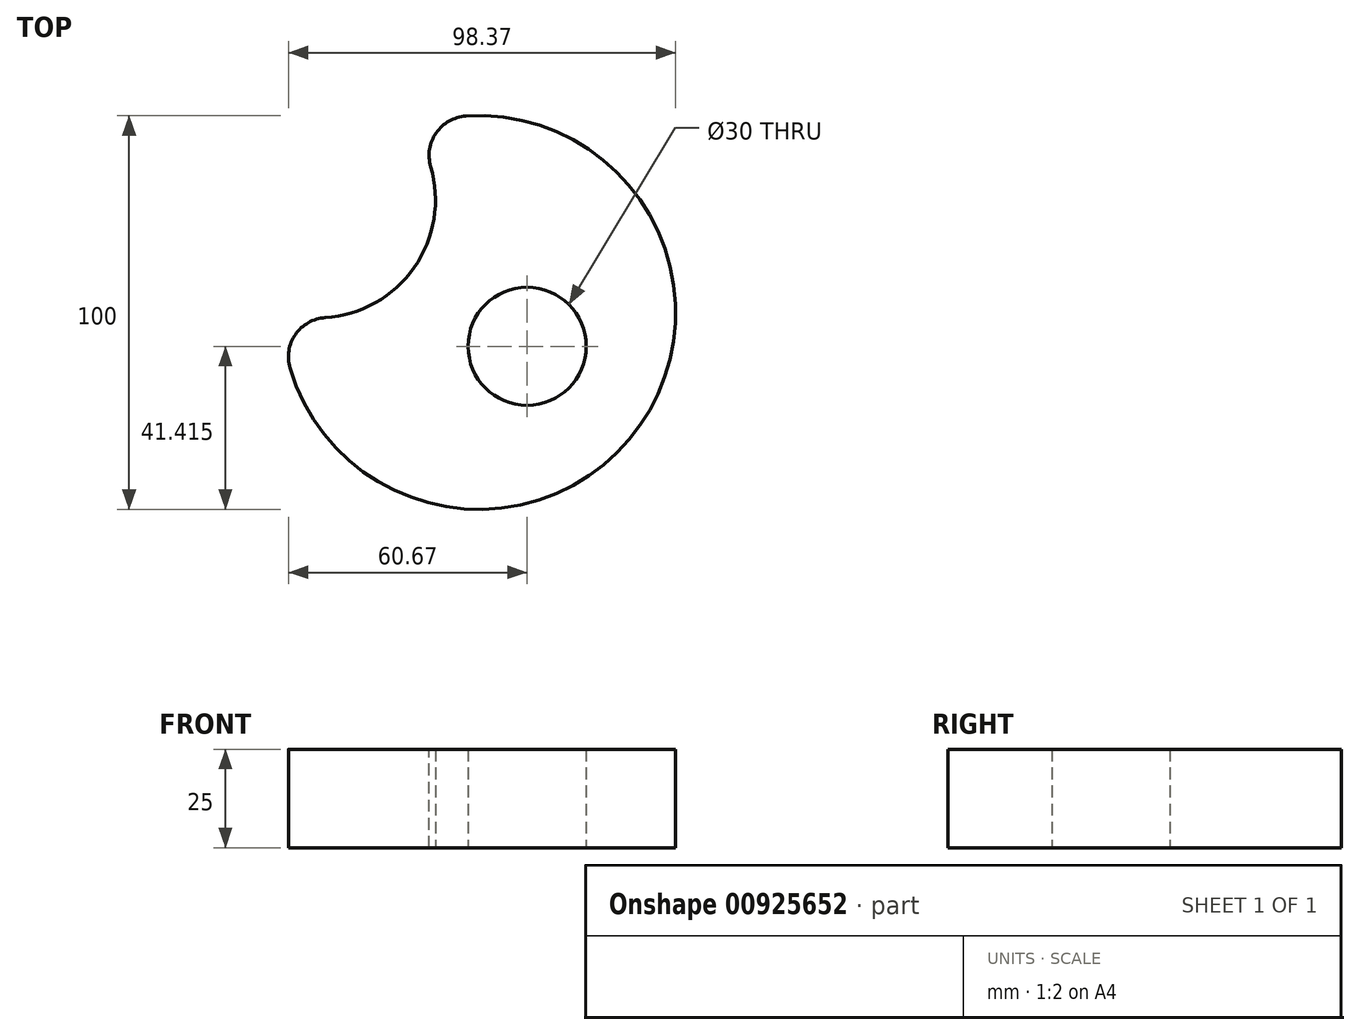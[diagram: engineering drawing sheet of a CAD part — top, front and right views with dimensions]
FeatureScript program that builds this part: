
annotation { "Feature Type Name" : "Feature", "Feature Type Description" : "" }
export const myFeature = defineFeature(function(context is Context, id is Id, definition is map)
    precondition{}
    {
        {
            var Q0;
            Q0=qCreatedBy(makeId("Top.planeOp"),FACE);
            var sketch = newSketch(context, id + "F0", { "sketchPlane" : qUnion([Q0])});
            skArc(sketch, "E0", {"start": v(-50, 0) * mm, "mid": v(41, -28.62) * mm, "end": v(-17.24, 46.93) * mm});
            skArc(sketch, "E1", {"start": v(-50, 0) * mm, "mid": v(-16.4, 11.45) * mm, "end": v(-17.24, 46.93) * mm});
            skLineSegment(sketch, "E2", {"start": v(-41, 28.62) * mm, "end": v(0, 0) * mm});
            skCircle(sketch, "E3", {"center": v(12.3, -8.59) * mm, "radius": 15 * mm});
            skSolve(sketch);
        }
        {
            var Q0;
            Q0=makeQuery(id+"F0.imprint","IMPRINT",FACE,{"disambiguationData":[TD([[makeQuery(id+"F0.imprint","IMPRINT",EDGE,{"derivedFrom":sQuery(id+"F0.wireOp",EDGE,"E0")}),1.0]])]});
            extrude(context, id + "F1", {"entities" : qUnion([Q0]), "depth" : 25 * mm, "offsetDistance" : 25 * mm});
        }
        {
            var Q0;
            {var subQ0=sQuery(id+"F0.wireOp",EDGE,"E1");var subQ1=sQuery(id+"F0.wireOp",EDGE,"E0");Q0=makeQuery(id+"F1.opExtrude","SWEPT_EDGE",EDGE,{"disambiguationData":[OSD([subQ1,subQ0]),TDD([makeQuery(id+"F0.imprint","INTERSECT",VERTEX,{"disambiguationData":[OD(1.0)],"derivedFrom":[subQ1,subQ0]})])]});}
            var Q1;
            {var subQ0=sQuery(id+"F0.wireOp",EDGE,"E1");var subQ1=sQuery(id+"F0.wireOp",EDGE,"E0");Q1=makeQuery(id+"F1.opExtrude","SWEPT_EDGE",EDGE,{"disambiguationData":[OSD([subQ1,subQ0]),TDD([makeQuery(id+"F0.imprint","INTERSECT",VERTEX,{"disambiguationData":[OD(0.0)],"derivedFrom":[subQ1,subQ0]})])]});}
            fillet(context, id + "F2", {"entities" : qUnion([Q0, Q1]), "radius" : 10 * mm, "tangentPropagation" : true, "allowEdgeOverflow" : false});
        }
    });
